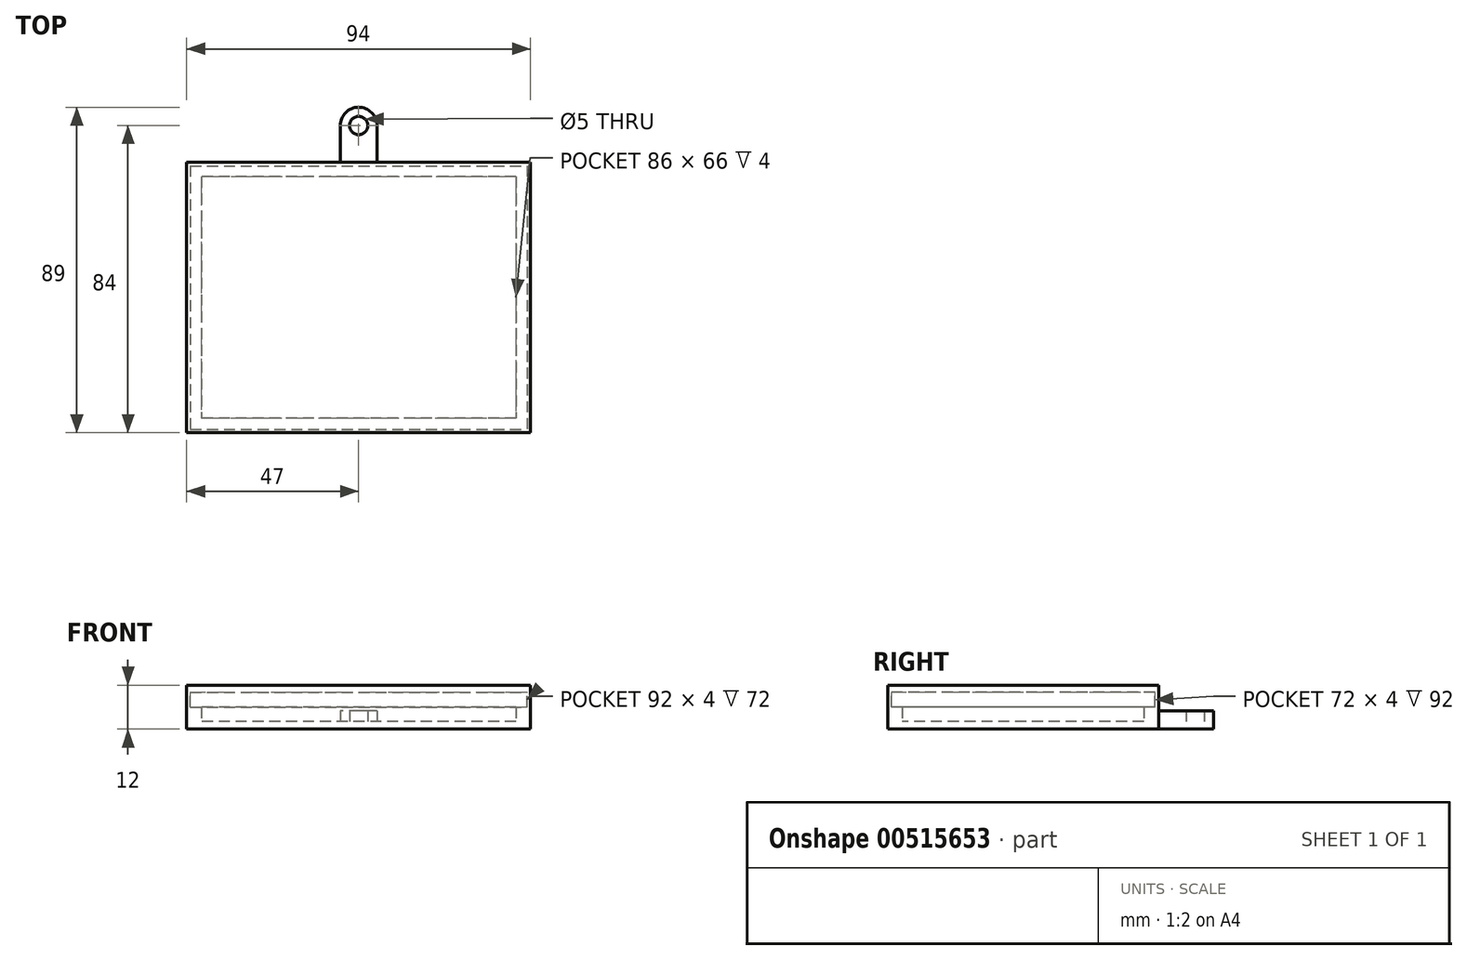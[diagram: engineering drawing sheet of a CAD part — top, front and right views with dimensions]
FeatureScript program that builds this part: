
annotation { "Feature Type Name" : "Feature", "Feature Type Description" : "" }
export const myFeature = defineFeature(function(context is Context, id is Id, definition is map)
    precondition{}
    {
        {
            var Q0;
            Q0=qCreatedBy(makeId("Top.planeOp"),FACE);
            var sketch = newSketch(context, id + "F0", { "sketchPlane" : qUnion([Q0])});
            skLineSegment(sketch, "E0.bottom", {"start": v(43, 33) * mm, "end": v(-43, 33) * mm});
            skLineSegment(sketch, "E0.top", {"start": v(43, -33) * mm, "end": v(-43, -33) * mm});
            skLineSegment(sketch, "E0.left", {"start": v(43, 33) * mm, "end": v(43, -33) * mm});
            skLineSegment(sketch, "E0.right", {"start": v(-43, 33) * mm, "end": v(-43, -33) * mm});
            skPoint(sketch, "E0.middle", {"position": v(0, 0) * mm});
            skLineSegment(sketch, "E1.bottom", {"start": v(47, 37) * mm, "end": v(-47, 37) * mm});
            skLineSegment(sketch, "E1.top", {"start": v(47, -37) * mm, "end": v(-47, -37) * mm});
            skLineSegment(sketch, "E1.left", {"start": v(47, 37) * mm, "end": v(47, -37) * mm});
            skLineSegment(sketch, "E1.right", {"start": v(-47, 37) * mm, "end": v(-47, -37) * mm});
            skPoint(sketch, "E2.endSnap0", {"position": v(0, 37) * mm});
            skCircle(sketch, "E3", {"center": v(0, 47) * mm, "radius": 5 * mm});
            skLineSegment(sketch, "E4", {"start": v(-5, 47) * mm, "end": v(-5, 37) * mm});
            skLineSegment(sketch, "E5", {"start": v(5, 47) * mm, "end": v(5, 37) * mm});
            skCircle(sketch, "E6", {"center": v(0, 47) * mm, "radius": 2.5 * mm});
            skSolve(sketch);
        }
        {
            var Q0;
            Q0=makeQuery(id+"F0.imprint","IMPRINT",FACE,{"disambiguationData":[TD([[makeQuery(id+"F0.imprint","IMPRINT",EDGE,{"derivedFrom":sQuery(id+"F0.wireOp",EDGE,"E0.bottom")}),1.0]])]});
            extrude(context, id + "F1", {"entities" : qUnion([Q0]), "depth" : 2 * mm, "offsetDistance" : 25 * mm});
        }
        {
            var Q0;
            Q0=makeQuery(id+"F0.imprint","IMPRINT",FACE,{"disambiguationData":[TD([[makeQuery(id+"F0.imprint","IMPRINT",EDGE,{"derivedFrom":sQuery(id+"F0.wireOp",EDGE,"E0.bottom")}),-1.0]])]});
            extrude(context, id + "F2", {"entities" : qUnion([Q0]), "operationType" : NewBodyOperationType.ADD, "depth" : 10 * mm, "offsetDistance" : 25 * mm});
        }
        {
            var Q0;
            Q0=makeQuery(id+"F2.opExtrude","CAP_FACE",FACE,{"disambiguationData":[OSD([sQuery(id+"F0.wireOp",EDGE,"E0.bottom"),sQuery(id+"F0.wireOp",EDGE,"E0.top"),sQuery(id+"F0.wireOp",EDGE,"E0.left"),sQuery(id+"F0.wireOp",EDGE,"E0.right"),sQuery(id+"F0.wireOp",EDGE,"E1.bottom"),sQuery(id+"F0.wireOp",EDGE,"E1.top"),sQuery(id+"F0.wireOp",EDGE,"E1.left"),sQuery(id+"F0.wireOp",EDGE,"E1.right")])],"isStart":false});
            var sketch = newSketch(context, id + "F3", { "sketchPlane" : qUnion([Q0])});
            skLineSegment(sketch, "E7.bottom", {"start": v(-46, 36) * mm, "end": v(46, 36) * mm});
            skLineSegment(sketch, "E7.top", {"start": v(-46, -36) * mm, "end": v(46, -36) * mm});
            skLineSegment(sketch, "E7.left", {"start": v(-46, 36) * mm, "end": v(-46, -36) * mm});
            skLineSegment(sketch, "E7.right", {"start": v(46, 36) * mm, "end": v(46, -36) * mm});
            skSolve(sketch);
        }
        {
            var Q0;
            Q0=makeQuery(id+"F3.imprint","IMPRINT",FACE,{"disambiguationData":[TD([[makeQuery(id+"F3.imprint","IMPRINT",EDGE,{"derivedFrom":sQuery(id+"F3.wireOp",EDGE,"E7.bottom")}),-1.0]])]});
            extrude(context, id + "F4", {"entities" : qUnion([Q0]), "operationType" : NewBodyOperationType.REMOVE, "oppositeDirection" : true, "depth" : 4 * mm, "offsetDistance" : 25 * mm});
        }
        {
            var Q0;
            Q0=makeQuery(id+"F2.opExtrude","CAP_FACE",FACE,{"disambiguationData":[OSD([sQuery(id+"F0.wireOp",EDGE,"E0.bottom"),sQuery(id+"F0.wireOp",EDGE,"E0.top"),sQuery(id+"F0.wireOp",EDGE,"E0.left"),sQuery(id+"F0.wireOp",EDGE,"E0.right"),sQuery(id+"F0.wireOp",EDGE,"E1.bottom"),sQuery(id+"F0.wireOp",EDGE,"E1.top"),sQuery(id+"F0.wireOp",EDGE,"E1.left"),sQuery(id+"F0.wireOp",EDGE,"E1.right")])],"isStart":false});
            var sketch = newSketch(context, id + "F5", { "sketchPlane" : qUnion([Q0])});
            skLineSegment(sketch, "E8", {"start": v(-46, -36) * mm, "end": v(-46, -34) * mm});
            skLineSegment(sketch, "E9", {"start": v(-46, -34) * mm, "end": v(46, -34) * mm});
            skLineSegment(sketch, "E10", {"start": v(46, 36) * mm, "end": v(46, 34) * mm});
            skLineSegment(sketch, "E11", {"start": v(46, 34) * mm, "end": v(-46, 34) * mm});
            skLineSegment(sketch, "E12", {"start": v(-46, 36) * mm, "end": v(-44, 36) * mm});
            skLineSegment(sketch, "E13", {"start": v(-44, 36) * mm, "end": v(-44, -36) * mm});
            skLineSegment(sketch, "E14", {"start": v(46, 36) * mm, "end": v(44, 36) * mm});
            skLineSegment(sketch, "E15", {"start": v(44, 36) * mm, "end": v(44, -36) * mm});
            skSolve(sketch);
        }
        {
            var Q0;
            {var subQ1=makeQuery(id+"F4.boolean.opBoolean","COPY",EDGE,{"derivedFrom":makeQuery(id+"F4.opExtrude","CAP_EDGE",EDGE,{"disambiguationData":[OSD([sQuery(id+"F3.wireOp",EDGE,"E7.left")])],"isStart":true})});var subQ5=sQuery(id+"F5.wireOp",EDGE,"E11");var subQ6=makeQuery(id+"F5.imprint","INTERSECT",VERTEX,{"derivedFrom":[subQ1,subQ5]});Q0=makeQuery(id+"F5.imprint","IMPRINT",FACE,{"disambiguationData":[TD([[makeQuery(id+"F5.imprint","IMPRINT",EDGE,{"disambiguationData":[TD([[subQ6,1.0]])],"derivedFrom":subQ5}),1.0]])]});}
            var Q1;
            {var subQ5=sQuery(id+"F5.wireOp",EDGE,"E12");Q1=makeQuery(id+"F5.imprint","IMPRINT",FACE,{"disambiguationData":[TD([[makeQuery(id+"F5.imprint","IMPRINT",EDGE,{"derivedFrom":subQ5}),-1.0]])]});}
            var Q2;
            {var subQ0=sQuery(id+"F5.wireOp",EDGE,"E15");var subQ1=sQuery(id+"F5.wireOp",EDGE,"E11");var subQ2=makeQuery(id+"F5.imprint","INTERSECT",VERTEX,{"derivedFrom":[subQ1,subQ0]});Q2=makeQuery(id+"F5.imprint","IMPRINT",FACE,{"disambiguationData":[TD([[makeQuery(id+"F5.imprint","IMPRINT",EDGE,{"disambiguationData":[TD([[subQ2,-1.0]])],"derivedFrom":subQ1}),-1.0]])]});}
            var Q3;
            {var subQ0=sQuery(id+"F5.wireOp",EDGE,"E10");Q3=makeQuery(id+"F5.imprint","IMPRINT",FACE,{"disambiguationData":[TD([[makeQuery(id+"F5.imprint","IMPRINT",EDGE,{"derivedFrom":subQ0}),-1.0]])]});}
            var Q4;
            {var subQ0=sQuery(id+"F5.wireOp",EDGE,"E9");var subQ1=makeQuery(id+"F4.boolean.opBoolean","COPY",EDGE,{"derivedFrom":makeQuery(id+"F4.opExtrude","CAP_EDGE",EDGE,{"disambiguationData":[OSD([sQuery(id+"F3.wireOp",EDGE,"E7.right")])],"isStart":true})});var subQ2=makeQuery(id+"F5.imprint","INTERSECT",VERTEX,{"derivedFrom":[subQ1,subQ0]});Q4=makeQuery(id+"F5.imprint","IMPRINT",FACE,{"disambiguationData":[TD([[makeQuery(id+"F5.imprint","IMPRINT",EDGE,{"disambiguationData":[TD([[subQ2,1.0]])],"derivedFrom":subQ0}),1.0]])]});}
            var Q5;
            {var subQ0=sQuery(id+"F5.wireOp",EDGE,"E13");var subQ1=sQuery(id+"F5.wireOp",EDGE,"E9");var subQ2=makeQuery(id+"F5.imprint","INTERSECT",VERTEX,{"derivedFrom":[subQ1,subQ0]});Q5=makeQuery(id+"F5.imprint","IMPRINT",FACE,{"disambiguationData":[TD([[makeQuery(id+"F5.imprint","IMPRINT",EDGE,{"disambiguationData":[TD([[subQ2,-1.0]])],"derivedFrom":subQ1}),-1.0]])]});}
            var Q6;
            {var subQ0=sQuery(id+"F5.wireOp",EDGE,"E9");var subQ1=makeQuery(id+"F4.boolean.opBoolean","COPY",EDGE,{"derivedFrom":makeQuery(id+"F4.opExtrude","CAP_EDGE",EDGE,{"disambiguationData":[OSD([sQuery(id+"F3.wireOp",EDGE,"E7.right")])],"isStart":true})});var subQ2=makeQuery(id+"F5.imprint","INTERSECT",VERTEX,{"derivedFrom":[subQ1,subQ0]});Q6=makeQuery(id+"F5.imprint","IMPRINT",FACE,{"disambiguationData":[TD([[makeQuery(id+"F5.imprint","IMPRINT",EDGE,{"disambiguationData":[TD([[subQ2,1.0]])],"derivedFrom":subQ0}),-1.0]])]});}
            var Q7;
            {var subQ0=sQuery(id+"F5.wireOp",EDGE,"E8");Q7=makeQuery(id+"F5.imprint","IMPRINT",FACE,{"disambiguationData":[TD([[makeQuery(id+"F5.imprint","IMPRINT",EDGE,{"derivedFrom":subQ0}),1.0]])]});}
            var Q8;
            {var subQ0=sQuery(id+"F5.wireOp",EDGE,"E8");Q8=makeQuery(id+"F5.imprint","IMPRINT",FACE,{"disambiguationData":[TD([[makeQuery(id+"F5.imprint","IMPRINT",EDGE,{"derivedFrom":subQ0}),-1.0]])]});}
            extrude(context, id + "F6", {"entities" : qUnion([Q0, Q1, Q2, Q3, Q4, Q5, Q6, Q7, Q8]), "operationType" : NewBodyOperationType.ADD, "depth" : 2 * mm, "offsetDistance" : 25 * mm});
        }
        {
            var Q0;
            {var subQ0=sQuery(id+"F0.wireOp",EDGE,"E4");Q0=makeQuery(id+"F0.imprint","IMPRINT",FACE,{"disambiguationData":[TD([[makeQuery(id+"F0.imprint","IMPRINT",EDGE,{"derivedFrom":subQ0}),1.0]])]});}
            var Q1;
            Q1=makeQuery(id+"F0.imprint","IMPRINT",FACE,{"disambiguationData":[TD([[makeQuery(id+"F0.imprint","IMPRINT",EDGE,{"derivedFrom":sQuery(id+"F0.wireOp",EDGE,"E6")}),-1.0]])]});
            extrude(context, id + "F7", {"entities" : qUnion([Q0, Q1]), "operationType" : NewBodyOperationType.ADD, "depth" : 5 * mm, "offsetDistance" : 25 * mm});
        }
    });
